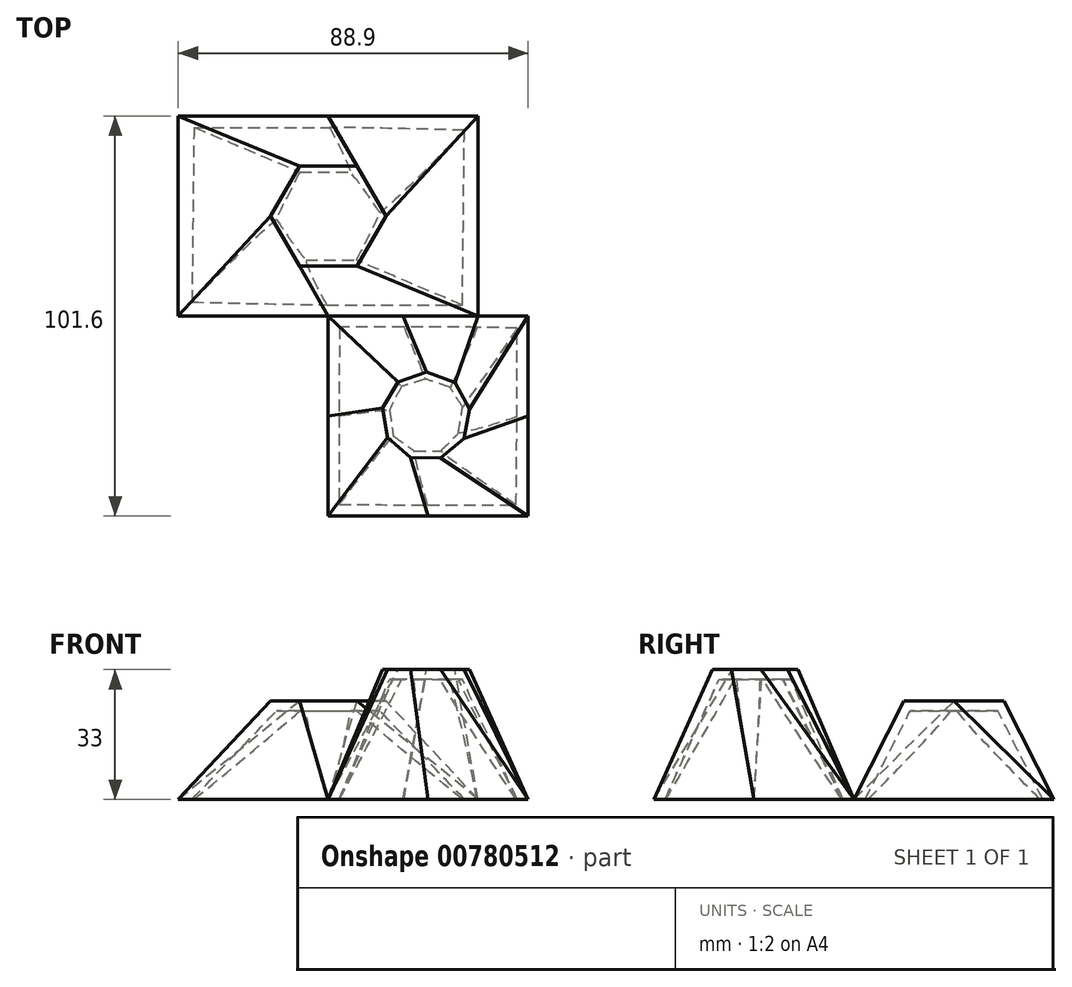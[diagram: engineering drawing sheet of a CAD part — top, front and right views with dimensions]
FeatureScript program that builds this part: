
annotation { "Feature Type Name" : "Feature", "Feature Type Description" : "" }
export const myFeature = defineFeature(function(context is Context, id is Id, definition is map)
    precondition{}
    {
        {
            var Q0;
            Q0=qCreatedBy(makeId("Top.planeOp"),FACE);
            var sketch = newSketch(context, id + "F0", { "sketchPlane" : qUnion([Q0])});
            skLineSegment(sketch, "E0", {"start": v(0, 0) * mm, "end": v(76.2, 0) * mm});
            skLineSegment(sketch, "E1", {"start": v(76.2, 0) * mm, "end": v(76.2, -50.8) * mm});
            skLineSegment(sketch, "E2", {"start": v(0, 0) * mm, "end": v(0, -50.8) * mm});
            skLineSegment(sketch, "E3", {"start": v(0, -50.8) * mm, "end": v(76.2, -50.8) * mm});
            skLineSegment(sketch, "E4", {"start": v(38.1, -50.8) * mm, "end": v(38.1, -101.6) * mm});
            skLineSegment(sketch, "E5", {"start": v(38.1, -101.6) * mm, "end": v(88.9, -101.6) * mm});
            skLineSegment(sketch, "E6", {"start": v(88.9, -101.6) * mm, "end": v(88.9, -50.8) * mm});
            skLineSegment(sketch, "E7", {"start": v(88.9, -50.8) * mm, "end": v(76.2, -50.8) * mm});
            skSolve(sketch);
        }
        {
            var Q0;
            Q0=makeQuery(id+"F0.imprint","IMPRINT",FACE,{"disambiguationData":[TD([[makeQuery(id+"F0.imprint","IMPRINT",EDGE,{"derivedFrom":sQuery(id+"F0.wireOp",EDGE,"E0")}),-1.0]])]});
            cPlane(context, id + "F1", {"entities" : qUnion([Q0]), "cplaneType" : CPlaneType.OFFSET, "offset" : 25 * mm, "width" : 152.4 * mm, "height" : 152.4 * mm});
        }
        {
            var Q0;
            Q0=qCreatedBy(id+"F1.planeOp",FACE);
            var sketch = newSketch(context, id + "F2", { "sketchPlane" : qUnion([Q0])});
            skPoint(sketch, "E8.middle", {"position": v(38.1, -25.4) * mm});
            skLineSegment(sketch, "E9.0", {"start": v(30.77, -12.7) * mm, "end": v(45.43, -12.7) * mm});
            skLineSegment(sketch, "E9.1", {"start": v(45.43, -12.7) * mm, "end": v(52.76, -25.4) * mm});
            skLineSegment(sketch, "E9.2", {"start": v(52.76, -25.4) * mm, "end": v(45.43, -38.1) * mm});
            skLineSegment(sketch, "E9.3", {"start": v(45.43, -38.1) * mm, "end": v(30.77, -38.1) * mm});
            skLineSegment(sketch, "E9.4", {"start": v(30.77, -38.1) * mm, "end": v(23.44, -25.4) * mm});
            skLineSegment(sketch, "E9.5", {"start": v(23.44, -25.4) * mm, "end": v(30.77, -12.7) * mm});
            skPoint(sketch, "E9.0.midPoint", {"position": v(38.1, -12.7) * mm});
            skSolve(sketch);
        }
        {
            var Q0;
            Q0=makeQuery(id+"F0.imprint","IMPRINT",FACE,{"disambiguationData":[TD([[makeQuery(id+"F0.imprint","IMPRINT",EDGE,{"derivedFrom":sQuery(id+"F0.wireOp",EDGE,"E0")}),-1.0]])]});
            var Q1;
            Q1=makeQuery(id+"F2.imprint","IMPRINT",FACE,{"disambiguationData":[TD([[makeQuery(id+"F2.imprint","IMPRINT",EDGE,{"derivedFrom":sQuery(id+"F2.wireOp",EDGE,"E9.0")}),-1.0]])]});
            loft(context, id + "F3", {"sheetProfilesArray" : [{ "sheetProfileEntities" : qUnion([Q0]) }, { "sheetProfileEntities" : qUnion([Q1]) }]});
        }
        {
            var Q0;
            {var subQ0=sQuery(id+"F0.wireOp",EDGE,"E4");Q0=makeQuery(id+"F0.imprint","IMPRINT",FACE,{"disambiguationData":[TD([[makeQuery(id+"F0.imprint","IMPRINT",EDGE,{"derivedFrom":subQ0}),1.0]])]});}
            cPlane(context, id + "F4", {"entities" : qUnion([Q0]), "cplaneType" : CPlaneType.OFFSET, "offset" : 33 * mm, "width" : 152.4 * mm, "height" : 152.4 * mm});
        }
        {
            var Q0;
            Q0=qCreatedBy(id+"F4.planeOp",FACE);
            var sketch = newSketch(context, id + "F5", { "sketchPlane" : qUnion([Q0])});
            skLineSegment(sketch, "E10", {"start": v(37.55, -50.81) * mm, "end": v(62.95, -50.81) * mm});
            skLineSegment(sketch, "E11", {"start": v(62.95, -50.81) * mm, "end": v(62.95, -76.21) * mm});
            skCircle(sketch, "E12.cCircle", {"center": v(62.95, -76.21) * mm, "radius": 10.54 * mm, "construction": true});
            skLineSegment(sketch, "E12.0", {"start": v(51.93, -74.12) * mm, "end": v(55.86, -67.53) * mm});
            skLineSegment(sketch, "E12.1", {"start": v(55.86, -67.53) * mm, "end": v(63.1, -65) * mm});
            skLineSegment(sketch, "E12.2", {"start": v(63.1, -65) * mm, "end": v(70.27, -67.72) * mm});
            skLineSegment(sketch, "E12.3", {"start": v(70.27, -67.72) * mm, "end": v(74.02, -74.41) * mm});
            skLineSegment(sketch, "E12.4", {"start": v(74.02, -74.41) * mm, "end": v(72.59, -81.95) * mm});
            skLineSegment(sketch, "E12.5", {"start": v(72.59, -81.95) * mm, "end": v(66.65, -86.8) * mm});
            skLineSegment(sketch, "E12.6", {"start": v(66.65, -86.8) * mm, "end": v(58.98, -86.7) * mm});
            skLineSegment(sketch, "E12.7", {"start": v(58.98, -86.7) * mm, "end": v(53.17, -81.7) * mm});
            skLineSegment(sketch, "E12.8", {"start": v(53.17, -81.7) * mm, "end": v(51.93, -74.12) * mm});
            skPoint(sketch, "E12.0.midPoint", {"position": v(53.9, -70.83) * mm});
            skSolve(sketch);
        }
        {
            var Q0;
            {var subQ0=sQuery(id+"F0.wireOp",EDGE,"E4");Q0=makeQuery(id+"F0.imprint","IMPRINT",FACE,{"disambiguationData":[TD([[makeQuery(id+"F0.imprint","IMPRINT",EDGE,{"derivedFrom":subQ0}),1.0]])]});}
            var Q1;
            {var subQ2=sQuery(id+"F5.wireOp",EDGE,"E12.0");Q1=makeQuery(id+"F5.imprint","IMPRINT",FACE,{"disambiguationData":[TD([[makeQuery(id+"F5.imprint","IMPRINT",EDGE,{"derivedFrom":subQ2}),-1.0]])]});}
            loft(context, id + "F6", {"sheetProfilesArray" : [{ "sheetProfileEntities" : qUnion([Q0]) }, { "sheetProfileEntities" : qUnion([Q1]) }]});
        }
        {
            var Q0;
            Q0=makeQuery(id+"F3.opLoft","CAP_FACE",FACE,{"disambiguationData":[OSD([makeQuery(id+"F0.imprint","IMPRINT",FACE,{"disambiguationData":[TD([[makeQuery(id+"F0.imprint","IMPRINT",EDGE,{"derivedFrom":sQuery(id+"F0.wireOp",EDGE,"E0")}),-1.0]])]})])],"isStart":true});
            var Q1;
            {var subQ0=sQuery(id+"F0.wireOp",EDGE,"E4");Q1=makeQuery(id+"F6.opLoft","CAP_FACE",FACE,{"disambiguationData":[OSD([makeQuery(id+"F0.imprint","IMPRINT",FACE,{"disambiguationData":[TD([[makeQuery(id+"F0.imprint","IMPRINT",EDGE,{"derivedFrom":subQ0}),1.0]])]})])],"isStart":true});}
            shell(context, id + "F7", {"entities" : qUnion([Q0, Q1]), "thickness" : 2.54 * mm});
        }
    });
